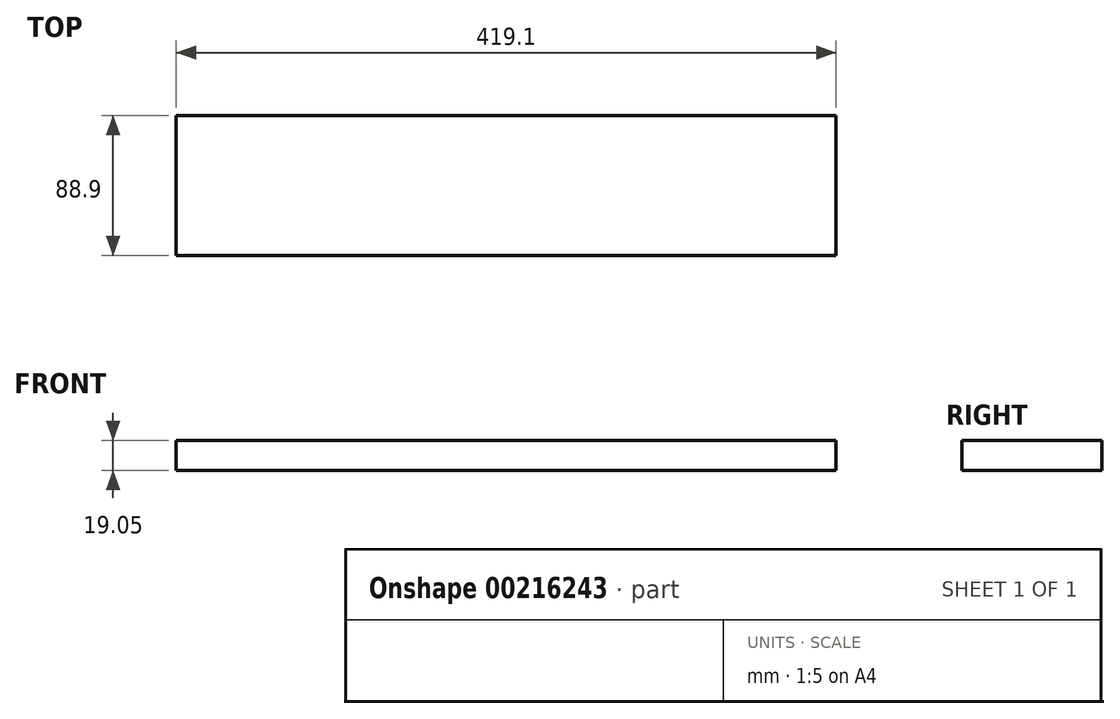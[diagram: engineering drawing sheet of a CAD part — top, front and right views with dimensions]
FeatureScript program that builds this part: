
annotation { "Feature Type Name" : "Feature", "Feature Type Description" : "" }
export const myFeature = defineFeature(function(context is Context, id is Id, definition is map)
    precondition{}
    {
        {
            var Q0;
            Q0=qCreatedBy(makeId("Top.planeOp"),FACE);
            var sketch = newSketch(context, id + "F0", { "sketchPlane" : qUnion([Q0])});
            skLineSegment(sketch, "E0", {"start": v(-5434.35, -858.57) * mm, "end": v(-5015.25, -858.57) * mm});
            skLineSegment(sketch, "E1", {"start": v(-5015.25, -858.57) * mm, "end": v(-5015.25, -769.67) * mm});
            skLineSegment(sketch, "E2", {"start": v(-5015.25, -769.67) * mm, "end": v(-5434.35, -769.67) * mm});
            skLineSegment(sketch, "E3", {"start": v(-5434.35, -769.67) * mm, "end": v(-5434.35, -858.57) * mm});
            skSolve(sketch);
        }
        {
            var Q0;
            Q0=makeQuery(id+"F0.imprint","IMPRINT",FACE,{"disambiguationData":[TD([[makeQuery(id+"F0.imprint","IMPRINT",EDGE,{"derivedFrom":sQuery(id+"F0.wireOp",EDGE,"E0")}),1.0]])]});
            extrude(context, id + "F1", {"entities" : qUnion([Q0]), "depth" : 19.05 * mm});
        }
    });
